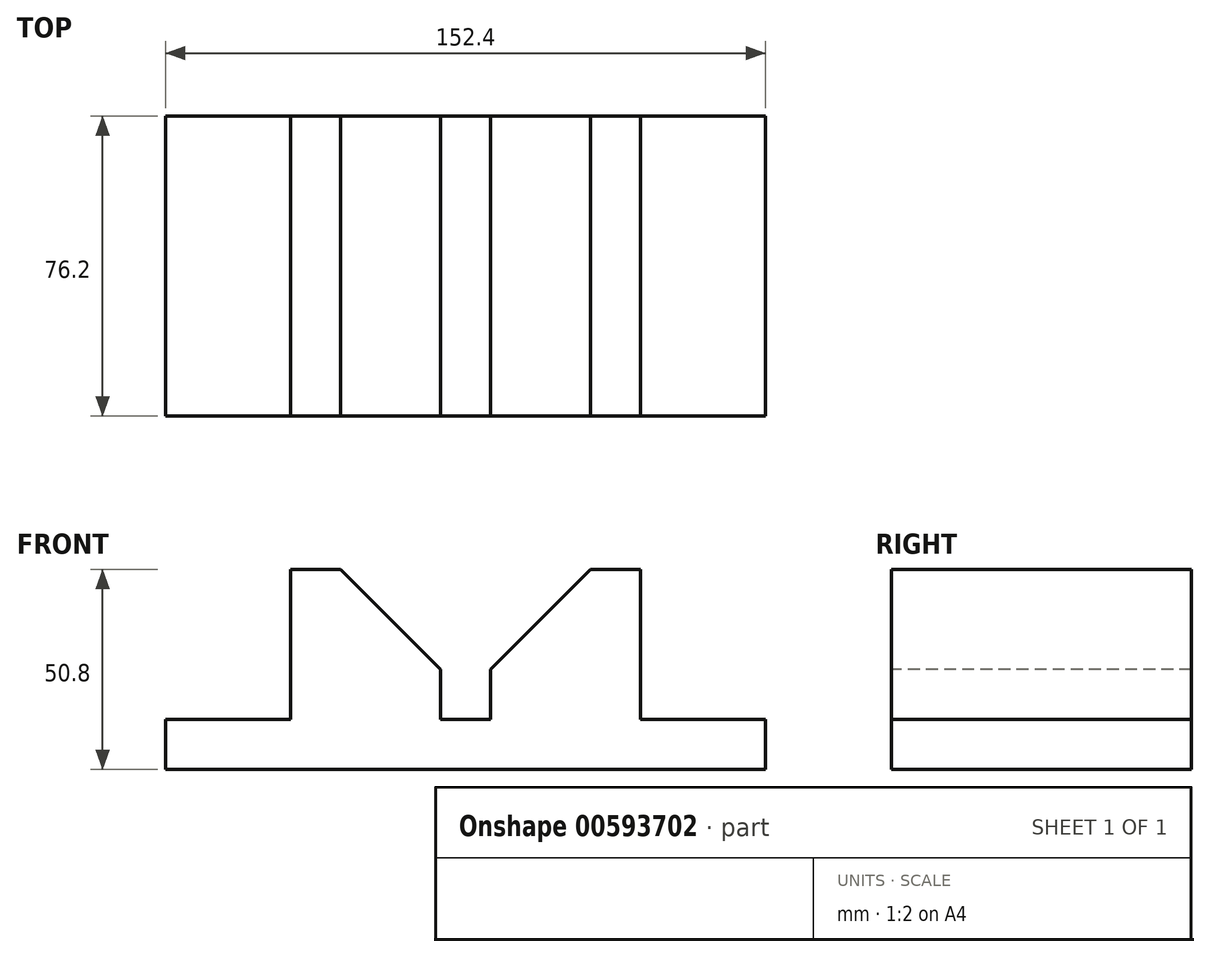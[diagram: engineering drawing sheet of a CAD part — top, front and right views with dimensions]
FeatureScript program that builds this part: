
annotation { "Feature Type Name" : "Feature", "Feature Type Description" : "" }
export const myFeature = defineFeature(function(context is Context, id is Id, definition is map)
    precondition{}
    {
        {
            var Q0;
            Q0=qCreatedBy(makeId("Front.planeOp"),FACE);
            var sketch = newSketch(context, id + "F0", { "sketchPlane" : qUnion([Q0])});
            skLineSegment(sketch, "E0", {"start": v(0, 0) * mm, "end": v(152.4, 0) * mm});
            skLineSegment(sketch, "E1", {"start": v(152.4, 0) * mm, "end": v(152.4, 50.8) * mm});
            skLineSegment(sketch, "E2", {"start": v(152.4, 50.8) * mm, "end": v(0, 50.8) * mm});
            skLineSegment(sketch, "E3", {"start": v(0, 50.8) * mm, "end": v(0, 0) * mm});
            skSolve(sketch);
        }
        {
            var Q0;
            Q0=makeQuery(id+"F0.imprint","IMPRINT",FACE,{"disambiguationData":[TD([[makeQuery(id+"F0.imprint","IMPRINT",EDGE,{"derivedFrom":sQuery(id+"F0.wireOp",EDGE,"E0")}),1.0]])]});
            extrude(context, id + "F1", {"entities" : qUnion([Q0]), "oppositeDirection" : true, "depth" : 76.2 * mm, "offsetDistance" : 25.4 * mm});
        }
        {
            var Q0;
            Q0=makeQuery(id+"F1.opExtrude","CAP_FACE",FACE,{"disambiguationData":[OSD([sQuery(id+"F0.wireOp",EDGE,"E0"),sQuery(id+"F0.wireOp",EDGE,"E1"),sQuery(id+"F0.wireOp",EDGE,"E2"),sQuery(id+"F0.wireOp",EDGE,"E3")])],"isStart":true});
            var sketch = newSketch(context, id + "F2", { "sketchPlane" : qUnion([Q0])});
            skLineSegment(sketch, "E4", {"start": v(152.4, 50.8) * mm, "end": v(120.65, 50.8) * mm});
            skLineSegment(sketch, "E5", {"start": v(120.65, 50.8) * mm, "end": v(120.65, 6.35) * mm});
            skLineSegment(sketch, "E6", {"start": v(120.65, 6.35) * mm, "end": v(152.4, 6.35) * mm});
            skLineSegment(sketch, "E7", {"start": v(0, 50.8) * mm, "end": v(31.75, 50.8) * mm});
            skLineSegment(sketch, "E8", {"start": v(31.75, 50.8) * mm, "end": v(31.75, 6.35) * mm});
            skLineSegment(sketch, "E9", {"start": v(31.75, 6.35) * mm, "end": v(0, 6.35) * mm});
            skSolve(sketch);
        }
        {
            var Q0;
            {var subQ0=sQuery(id+"F2.wireOp",EDGE,"E7");Q0=makeQuery(id+"F2.imprint","IMPRINT",FACE,{"disambiguationData":[TD([[makeQuery(id+"F2.imprint","IMPRINT",EDGE,{"derivedFrom":subQ0}),1.0]])]});}
            var Q1;
            {var subQ0=sQuery(id+"F2.wireOp",EDGE,"E4");Q1=makeQuery(id+"F2.imprint","IMPRINT",FACE,{"disambiguationData":[TD([[makeQuery(id+"F2.imprint","IMPRINT",EDGE,{"derivedFrom":subQ0}),1.0]])]});}
            extrude(context, id + "F3", {"entities" : qUnion([Q0, Q1]), "operationType" : NewBodyOperationType.REMOVE, "oppositeDirection" : true, "depth" : 76.2 * mm, "offsetDistance" : 25.4 * mm});
        }
        {
            var Q0;
            Q0=makeQuery(id+"F1.opExtrude","SWEPT_FACE",FACE,{"disambiguationData":[OSD([sQuery(id+"F0.wireOp",EDGE,"E2")])]});
            var sketch = newSketch(context, id + "F4", { "sketchPlane" : qUnion([Q0])});
            skLineSegment(sketch, "E10", {"start": v(31.75, 0) * mm, "end": v(44.45, 0) * mm});
            skLineSegment(sketch, "E11", {"start": v(44.45, 0) * mm, "end": v(69.85, 0) * mm});
            skLineSegment(sketch, "E12", {"start": v(69.85, 0) * mm, "end": v(69.85, 76.2) * mm});
            skLineSegment(sketch, "E13", {"start": v(69.85, 76.2) * mm, "end": v(44.45, 76.2) * mm});
            skLineSegment(sketch, "E14", {"start": v(44.45, 76.2) * mm, "end": v(44.45, 0) * mm});
            skLineSegment(sketch, "E15", {"start": v(120.65, 0) * mm, "end": v(107.95, 0) * mm});
            skLineSegment(sketch, "E16", {"start": v(107.95, 0) * mm, "end": v(82.55, 0) * mm});
            skLineSegment(sketch, "E17", {"start": v(82.55, 0) * mm, "end": v(82.55, 76.2) * mm});
            skLineSegment(sketch, "E18", {"start": v(82.55, 76.2) * mm, "end": v(120.65, 76.2) * mm});
            skLineSegment(sketch, "E19", {"start": v(107.95, 0) * mm, "end": v(107.95, 76.2) * mm});
            skSolve(sketch);
        }
        {
            var Q0;
            {var subQ0=sQuery(id+"F4.wireOp",EDGE,"E12");Q0=makeQuery(id+"F4.imprint","IMPRINT",FACE,{"disambiguationData":[TD([[makeQuery(id+"F4.imprint","IMPRINT",EDGE,{"derivedFrom":subQ0}),-1.0]])]});}
            extrude(context, id + "F5", {"entities" : qUnion([Q0]), "operationType" : NewBodyOperationType.REMOVE, "oppositeDirection" : true, "depth" : 38.1 * mm, "offsetDistance" : 25.4 * mm});
        }
        {
            var Q0;
            Q0=makeQuery(id+"F1.opExtrude","CAP_FACE",FACE,{"disambiguationData":[OSD([sQuery(id+"F0.wireOp",EDGE,"E0"),sQuery(id+"F0.wireOp",EDGE,"E1"),sQuery(id+"F0.wireOp",EDGE,"E2"),sQuery(id+"F0.wireOp",EDGE,"E3")])],"isStart":true});
            var sketch = newSketch(context, id + "F6", { "sketchPlane" : qUnion([Q0])});
            skLineSegment(sketch, "E20", {"start": v(69.85, 12.7) * mm, "end": v(69.85, 25.4) * mm});
            skLineSegment(sketch, "E21", {"start": v(69.85, 25.4) * mm, "end": v(69.85, 50.8) * mm});
            skLineSegment(sketch, "E22", {"start": v(69.85, 50.8) * mm, "end": v(44.45, 50.8) * mm});
            skLineSegment(sketch, "E23", {"start": v(44.45, 50.8) * mm, "end": v(69.85, 25.4) * mm});
            skSolve(sketch);
        }
        {
            var Q0;
            Q0 = qSketchRegion(id + "F6", true);
            extrude(context, id + "F7", {"entities" : qUnion([Q0]), "operationType" : NewBodyOperationType.REMOVE, "oppositeDirection" : true, "depth" : 76.2 * mm, "offsetDistance" : 25.4 * mm});
        }
        {
            var Q0;
            Q0=makeQuery(id+"F1.opExtrude","CAP_FACE",FACE,{"disambiguationData":[OSD([sQuery(id+"F0.wireOp",EDGE,"E0"),sQuery(id+"F0.wireOp",EDGE,"E1"),sQuery(id+"F0.wireOp",EDGE,"E2"),sQuery(id+"F0.wireOp",EDGE,"E3")])],"isStart":true});
            var sketch = newSketch(context, id + "F8", { "sketchPlane" : qUnion([Q0])});
            skLineSegment(sketch, "E24", {"start": v(82.55, 12.7) * mm, "end": v(82.55, 25.4) * mm});
            skLineSegment(sketch, "E25", {"start": v(82.55, 25.4) * mm, "end": v(82.55, 50.8) * mm});
            skLineSegment(sketch, "E26", {"start": v(82.55, 50.8) * mm, "end": v(107.95, 50.8) * mm});
            skLineSegment(sketch, "E27", {"start": v(107.95, 50.8) * mm, "end": v(82.55, 25.4) * mm});
            skSolve(sketch);
        }
        {
            var Q0;
            Q0=makeQuery(id+"F8.imprint","IMPRINT",FACE,{"disambiguationData":[TD([[makeQuery(id+"F8.imprint","IMPRINT",EDGE,{"derivedFrom":sQuery(id+"F8.wireOp",EDGE,"E25")}),-1.0]])]});
            extrude(context, id + "F9", {"entities" : qUnion([Q0]), "operationType" : NewBodyOperationType.REMOVE, "oppositeDirection" : true, "depth" : 76.2 * mm, "offsetDistance" : 25.4 * mm});
        }
        {
            var Q0;
            Q0=makeQuery(id+"F3.boolean.opBoolean","COPY",FACE,{"derivedFrom":makeQuery(id+"F3.opExtrude","SWEPT_FACE",FACE,{"disambiguationData":[OSD([sQuery(id+"F2.wireOp",EDGE,"E6")])]})});
            extrude(context, id + "F10", {"entities" : qUnion([Q0]), "operationType" : NewBodyOperationType.ADD, "depth" : 6.35 * mm, "offsetDistance" : 25.4 * mm});
        }
        {
            var Q0;
            Q0=makeQuery(id+"F3.boolean.opBoolean","COPY",FACE,{"derivedFrom":makeQuery(id+"F3.opExtrude","SWEPT_FACE",FACE,{"disambiguationData":[OSD([sQuery(id+"F2.wireOp",EDGE,"E9")])]})});
            extrude(context, id + "F11", {"entities" : qUnion([Q0]), "operationType" : NewBodyOperationType.ADD, "depth" : 6.35 * mm, "offsetDistance" : 25.4 * mm});
        }
    });
